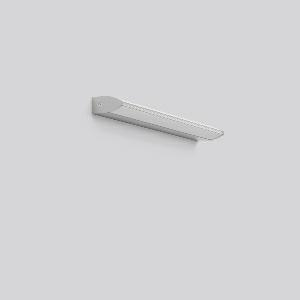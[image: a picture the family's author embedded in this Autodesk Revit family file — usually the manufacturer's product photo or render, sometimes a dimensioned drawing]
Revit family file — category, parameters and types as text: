
# Revit family: lavano_uno_451198_000_76_f620
name_source: partatom
category: Lighting Fixtures
units: mm (PartAtom-declared; Revit-internal decimal feet)

## family parameters
Cut with Voids When Loaded = No
Host = Face
Light Source = No
Part Type = Normal
Room Calculation Point = No
Round Connector Dimension = Use Diameter
Shared = No

## types (1)
- LAVANO UNO (1 x LED Modul 830, 1250 lm, 3000)
    Apparent Load = 11 VA
    CIE Flux Codes = 36 62 83 77 100
    Color Rendering = 80
    Color Temperature = 3000
    Default Elevation = 1800 mm
    Description = Series: LAVANO UNO
Linear LED surface-mounted luminaire in an elegant design. Extruded aluminium profile base, lacquered. End caps aluminium, painted. Diffuser: plastic, opal, allows for brilliant glittering light along the lines of the ellipse. Suitable for Ceiling mounting, Wall (surface). 
Colour: white aluminium (RAL 9006)
Length: 580 mm
Width: 40 mm
Height: 83 mm
Lamp: LED
Socket: without socket
Colour temperature: 3000K
Colour rendering index (CRI): 80
System power: 11 W
Rated luminous flux: 1250 lm
Luminous efficiency: 114 lm/W
Control gear: Converter, dimmable, DALI
Protection class: I
Type of protection: IP 40
    Height = 83 mm
    Lamp = 1 x LED Modul 830
    Lamp Light Flux = 1250 lm
    Lamp count = 1
    Length = 580 mm
    Lifetime = 50000 h
    Luminous efficacy = 114 lm/W
    Manufacturer = RZB
    ModVariant = No
    Model = 451198.000.76
    Mounting Place = Ceiling, Wall
    Mounting Type = Surface mounted
    Number of Poles = 1
    OnlyDefault = Yes
    Power Factor = 1
    Product Name = LAVANO UNO
    Product group = Surface mounted ceiling and wall luminaires
    ProductGroupID = 305
    Protection Class = Protection class I
    Protection Degree = IP 40
    RLX_Detail_Level = 1
    RLX_Emergency_Light_Flux = 0 lm
    RLX_Emergency_Type = 0
    RLX_Emergency_Type_DB = No
    RlxData = <blob elided: 24833 chars, md5=86e34b1c>
    Socket = socket
    Standby Power = 0 W
    System Light Flux = 1250 lm
    System Power = 11 W
    Type Comments = Product without accessories
    Type Image = 451100.000.jpg
    URL = http://relux.com
    VarID = ---
    Voltage = 230 V
    Voltage Range = 220-240 V
    Weight = 0.00 kg
    Width = 40 mm  [stored 0.131234 ft]

note: [stored X ft] marks values corroborated as IEEE doubles in the binary element streams (Revit-internal decimal feet)

## geometry (parser evidence)
native form markers: Blend x4, Sweep x15
no freeform markers — native parametric forms only
